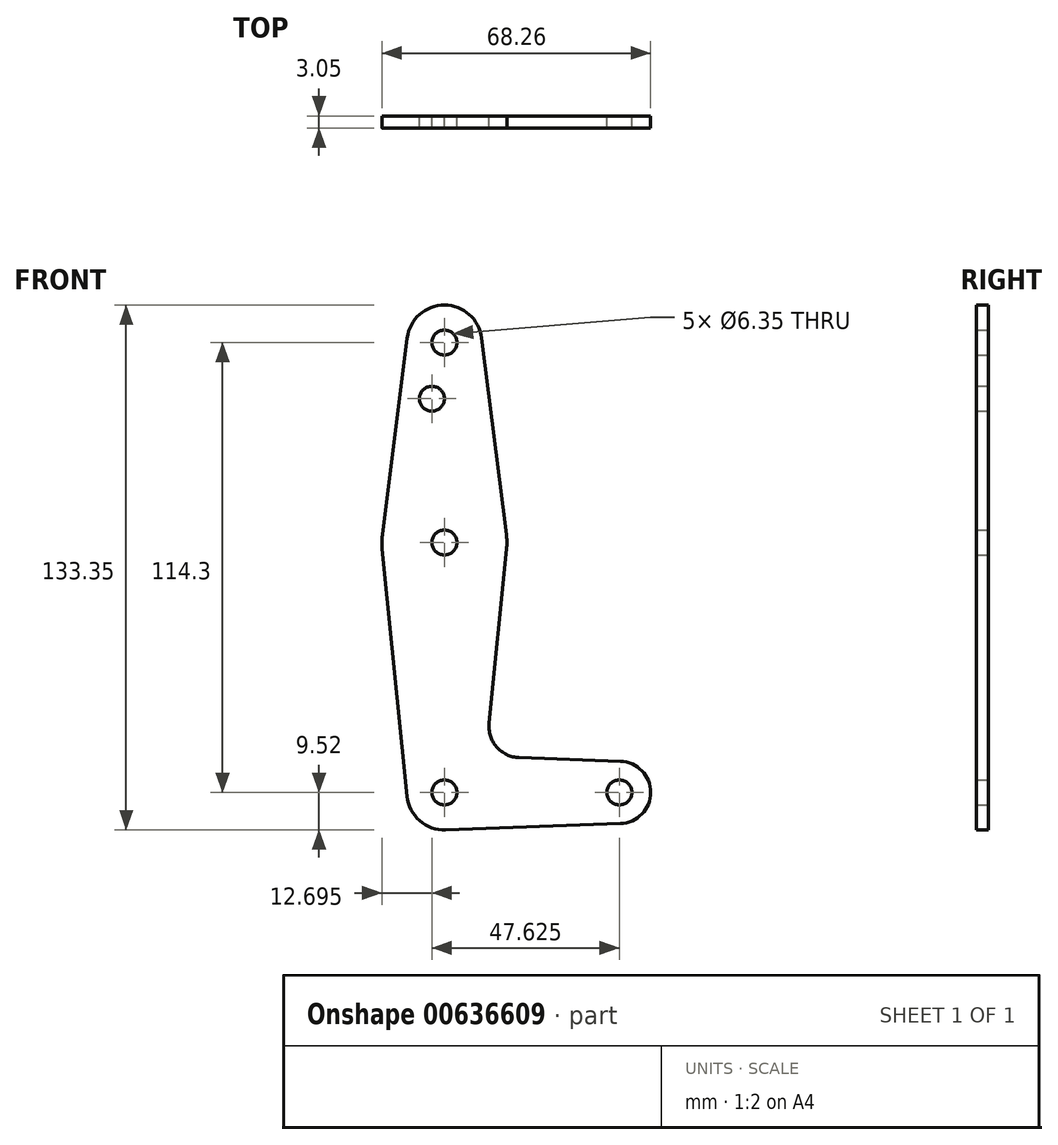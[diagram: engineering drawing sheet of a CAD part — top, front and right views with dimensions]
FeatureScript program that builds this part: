
annotation { "Feature Type Name" : "Feature", "Feature Type Description" : "" }
export const myFeature = defineFeature(function(context is Context, id is Id, definition is map)
    precondition{}
    {
        {
            var Q0;
            Q0=qCreatedBy(makeId("Front.planeOp"),FACE);
            var sketch = newSketch(context, id + "F0", { "sketchPlane" : qUnion([Q0])});
            skLineSegment(sketch, "E0", {"start": v(0, 0) * mm, "end": v(44.45, 0) * mm, "construction": true});
            skLineSegment(sketch, "E1", {"start": v(0, 0) * mm, "end": v(0, 114.3) * mm, "construction": true});
            skCircle(sketch, "E2", {"center": v(44.45, 0) * mm, "radius": 7.94 * mm});
            skCircle(sketch, "E3", {"center": v(0, 0) * mm, "radius": 9.53 * mm});
            skCircle(sketch, "E4", {"center": v(0, 114.3) * mm, "radius": 9.53 * mm});
            skCircle(sketch, "E5", {"center": v(0, 63.5) * mm, "radius": 15.88 * mm});
            skLineSegment(sketch, "E6", {"start": v(-9.45, 115.5) * mm, "end": v(-15.75, 65.48) * mm});
            skLineSegment(sketch, "E7", {"start": v(15.8, 61.91) * mm, "end": v(11.34, 17.6) * mm});
            skLineSegment(sketch, "E8", {"start": v(-15.8, 61.91) * mm, "end": v(-9.48, -0.95) * mm});
            skLineSegment(sketch, "E9", {"start": v(18.97, 8.85) * mm, "end": v(44.73, 7.93) * mm});
            skLineSegment(sketch, "E10", {"start": v(0.34, -9.52) * mm, "end": v(44.73, -7.93) * mm});
            skLineSegment(sketch, "E11", {"start": v(9.45, 115.5) * mm, "end": v(15.75, 65.48) * mm});
            skCircle(sketch, "E12", {"center": v(0, 114.3) * mm, "radius": 3.18 * mm});
            skCircle(sketch, "E13", {"center": v(0, 63.5) * mm, "radius": 3.18 * mm});
            skCircle(sketch, "E14", {"center": v(0, 0) * mm, "radius": 3.18 * mm});
            skCircle(sketch, "E15", {"center": v(44.45, 0) * mm, "radius": 3.18 * mm});
            skCircle(sketch, "E16", {"center": v(-3.18, 100.03) * mm, "radius": 3.18 * mm});
            skArc(sketch, "E17.filletArc", {"start": v(11.34, 17.6) * mm, "mid": v(13.26, 11.57) * mm, "end": v(18.97, 8.85) * mm});
            skSolve(sketch);
        }
        {
            var Q0;
            Q0 = qSketchRegion(id + "F0", true);
            extrude(context, id + "F1", {"entities" : qUnion([Q0]), "depth" : 3.05 * mm, "offsetDistance" : 25.4 * mm});
        }
    });
